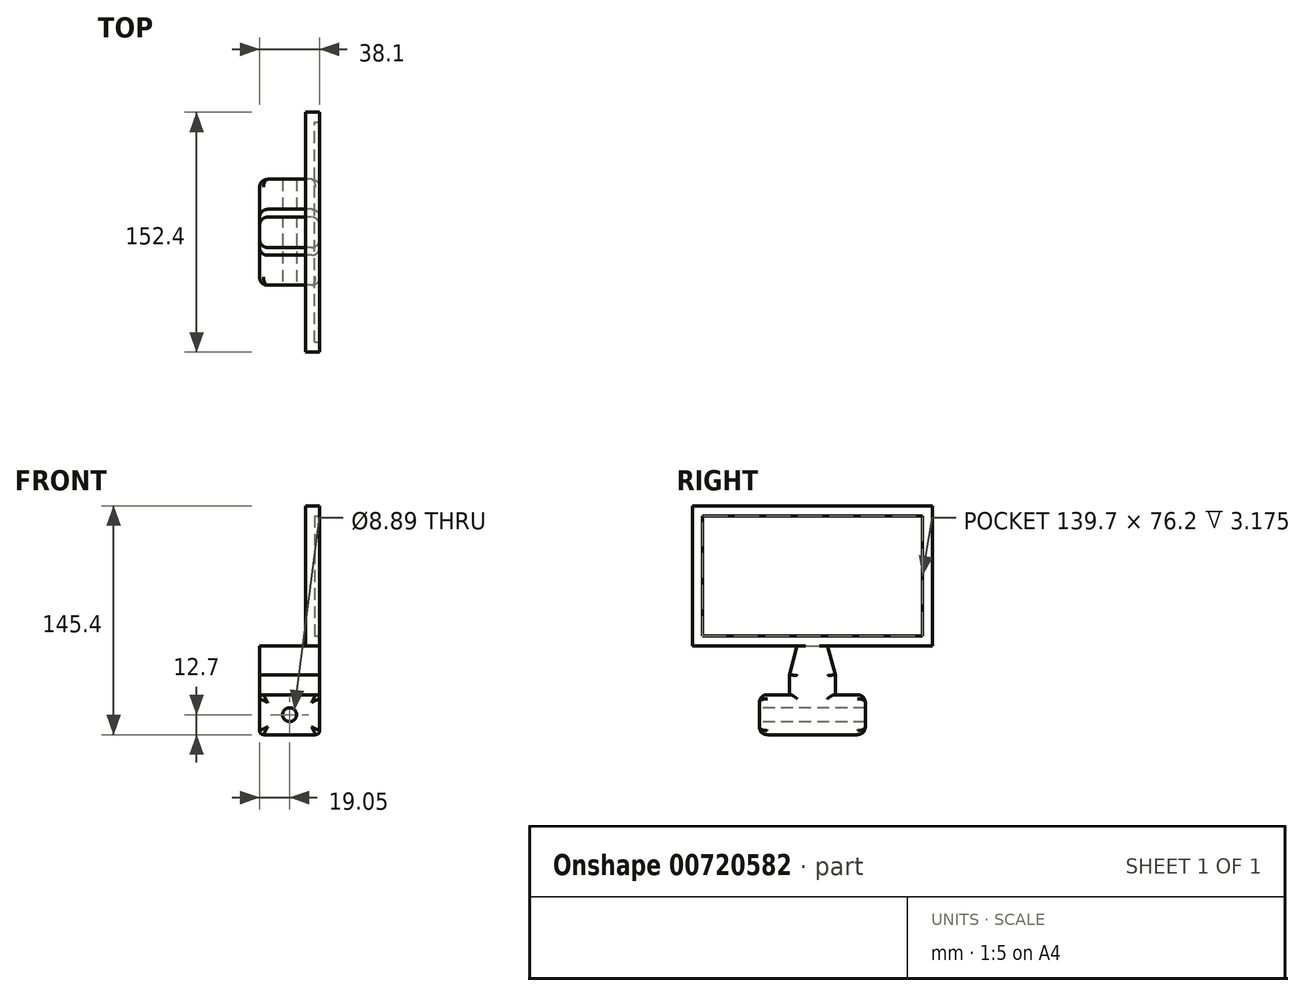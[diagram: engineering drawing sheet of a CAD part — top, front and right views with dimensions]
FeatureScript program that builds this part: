
annotation { "Feature Type Name" : "Feature", "Feature Type Description" : "" }
export const myFeature = defineFeature(function(context is Context, id is Id, definition is map)
    precondition{}
    {
        {
            var Q0;
            Q0=qCreatedBy(makeId("Right.planeOp"),FACE);
            var sketch = newSketch(context, id + "F0", { "sketchPlane" : qUnion([Q0])});
            skLineSegment(sketch, "E0.top", {"start": v(-67.31, 0) * mm, "end": v(0, 0) * mm});
            skLineSegment(sketch, "E0.left", {"start": v(-67.31, 25.4) * mm, "end": v(-67.31, 0) * mm});
            skLineSegment(sketch, "E0.right", {"start": v(0, 25.4) * mm, "end": v(0, 0) * mm});
            skLineSegment(sketch, "E1", {"start": v(-67.31, 25.4) * mm, "end": v(-48.26, 25.4) * mm});
            skLineSegment(sketch, "E2", {"start": v(0, 25.4) * mm, "end": v(-19.05, 25.4) * mm});
            skLineSegment(sketch, "E3", {"start": v(-48.26, 25.4) * mm, "end": v(-48.26, 38.1) * mm});
            skLineSegment(sketch, "E4", {"start": v(-19.05, 25.4) * mm, "end": v(-19.05, 38.1) * mm});
            skLineSegment(sketch, "E5", {"start": v(-48.26, 38.1) * mm, "end": v(-43.33, 56.5) * mm});
            skLineSegment(sketch, "E6", {"start": v(-19.05, 38.1) * mm, "end": v(-23.98, 56.5) * mm});
            skLineSegment(sketch, "E7", {"start": v(-43.33, 56.5) * mm, "end": v(-23.98, 56.5) * mm});
            skSolve(sketch);
        }
        {
            var Q0;
            Q0=makeQuery(id+"F0.imprint","IMPRINT",FACE,{"disambiguationData":[TD([[makeQuery(id+"F0.imprint","IMPRINT",EDGE,{"derivedFrom":sQuery(id+"F0.wireOp",EDGE,"E0.top")}),1.0]])]});
            extrude(context, id + "F1", {"entities" : qUnion([Q0]), "depth" : 38.1 * mm, "offsetDistance" : 25.4 * mm});
        }
        {
            var Q0;
            Q0=makeQuery(id+"F1.opExtrude","SWEPT_EDGE",EDGE,{"disambiguationData":[OSD([sQuery(id+"F0.wireOp",EDGE,"E0.left"),sQuery(id+"F0.wireOp",EDGE,"E1")])]});
            var Q1;
            Q1=makeQuery(id+"F1.opExtrude","CAP_EDGE",EDGE,{"disambiguationData":[OSD([sQuery(id+"F0.wireOp",EDGE,"E0.left")])],"isStart":false});
            var Q2;
            Q2=makeQuery(id+"F1.opExtrude","SWEPT_EDGE",EDGE,{"disambiguationData":[OSD([sQuery(id+"F0.wireOp",EDGE,"E0.top"),sQuery(id+"F0.wireOp",EDGE,"E0.left")])]});
            var Q3;
            Q3=makeQuery(id+"F1.opExtrude","SWEPT_FACE",FACE,{"disambiguationData":[OSD([sQuery(id+"F0.wireOp",EDGE,"E0.left")])]});
            var Q4;
            Q4=makeQuery(id+"F1.opExtrude","CAP_EDGE",EDGE,{"disambiguationData":[OSD([sQuery(id+"F0.wireOp",EDGE,"E0.right")])],"isStart":false});
            var Q5;
            Q5=makeQuery(id+"F1.opExtrude","SWEPT_EDGE",EDGE,{"disambiguationData":[OSD([sQuery(id+"F0.wireOp",EDGE,"E0.right"),sQuery(id+"F0.wireOp",EDGE,"E2")])]});
            var Q6;
            Q6=makeQuery(id+"F1.opExtrude","CAP_EDGE",EDGE,{"disambiguationData":[OSD([sQuery(id+"F0.wireOp",EDGE,"E0.right")])],"isStart":true});
            var Q7;
            Q7=makeQuery(id+"F1.opExtrude","SWEPT_EDGE",EDGE,{"disambiguationData":[OSD([sQuery(id+"F0.wireOp",EDGE,"E0.top"),sQuery(id+"F0.wireOp",EDGE,"E0.right")])]});
            fillet(context, id + "F2", {"entities" : qUnion([Q0, Q1, Q2, Q3, Q4, Q5, Q6, Q7]), "radius" : 5.08 * mm, "tangentPropagation" : true, "allowEdgeOverflow" : false});
        }
        {
            var Q0;
            Q0=makeQuery(id+"F1.opExtrude","SWEPT_FACE",FACE,{"disambiguationData":[OSD([sQuery(id+"F0.wireOp",EDGE,"E0.left")])]});
            var sketch = newSketch(context, id + "F3", { "sketchPlane" : qUnion([Q0])});
            skPoint(sketch, "E8", {"position": v(19.05, 12.7) * mm});
            skPoint(sketch, "E8.positionSnap0", {"position": v(19.05, 5.08) * mm});
            skSolve(sketch);
        }
        {
            var Q0;
            Q0=sQuery(id+"F3.wireOp",VERTEX,"E8");
            var Q1;
            Q1=makeQuery(id+"F1.opExtrude","SWEPT_BODY",BODY,{"disambiguationData":[OSD([sQuery(id+"F0.wireOp",EDGE,"E0.top"),sQuery(id+"F0.wireOp",EDGE,"E0.left"),sQuery(id+"F0.wireOp",EDGE,"E0.right"),sQuery(id+"F0.wireOp",EDGE,"E1"),sQuery(id+"F0.wireOp",EDGE,"E2"),sQuery(id+"F0.wireOp",EDGE,"E3"),sQuery(id+"F0.wireOp",EDGE,"E4"),sQuery(id+"F0.wireOp",EDGE,"E5"),sQuery(id+"F0.wireOp",EDGE,"E6"),sQuery(id+"F0.wireOp",EDGE,"E7")])]});
            hole(context, id + "F4", {"style" : HoleStyle.SIMPLE, "endStyle" : HoleEndStyle.THROUGH, "holeDiameter" : 8.9 * mm, "majorDiameter" : 6.35 * mm, "isTappedThrough" : true, "tappedDepth" : 12.7 * mm, "tapClearance" : 3, "startFromSketch" : true, "locations" : qUnion([Q0]), "scope" : qUnion([Q1])});
        }
        {
            var Q0;
            Q0=makeQuery(id+"F1.opExtrude","CAP_EDGE",EDGE,{"disambiguationData":[OSD([sQuery(id+"F0.wireOp",EDGE,"E3")])],"isStart":false});
            var Q1;
            Q1=makeQuery(id+"F1.opExtrude","CAP_EDGE",EDGE,{"disambiguationData":[OSD([sQuery(id+"F0.wireOp",EDGE,"E5")])],"isStart":false});
            var Q2;
            Q2=makeQuery(id+"F1.opExtrude","CAP_EDGE",EDGE,{"disambiguationData":[OSD([sQuery(id+"F0.wireOp",EDGE,"E6")])],"isStart":false});
            var Q3;
            Q3=makeQuery(id+"F1.opExtrude","CAP_EDGE",EDGE,{"disambiguationData":[OSD([sQuery(id+"F0.wireOp",EDGE,"E4")])],"isStart":false});
            var Q4;
            Q4=makeQuery(id+"F1.opExtrude","CAP_EDGE",EDGE,{"disambiguationData":[OSD([sQuery(id+"F0.wireOp",EDGE,"E3")])],"isStart":true});
            var Q5;
            Q5=makeQuery(id+"F1.opExtrude","CAP_EDGE",EDGE,{"disambiguationData":[OSD([sQuery(id+"F0.wireOp",EDGE,"E5")])],"isStart":true});
            var Q6;
            Q6=makeQuery(id+"F1.opExtrude","CAP_EDGE",EDGE,{"disambiguationData":[OSD([sQuery(id+"F0.wireOp",EDGE,"E4")])],"isStart":true});
            var Q7;
            Q7=makeQuery(id+"F1.opExtrude","CAP_EDGE",EDGE,{"disambiguationData":[OSD([sQuery(id+"F0.wireOp",EDGE,"E6")])],"isStart":true});
            fillet(context, id + "F5", {"entities" : qUnion([Q0, Q1, Q2, Q3, Q4, Q5, Q6, Q7]), "radius" : 5.08 * mm, "tangentPropagation" : true, "allowEdgeOverflow" : false});
        }
        {
            var Q0;
            Q0=makeQuery(id+"F1.opExtrude","CAP_FACE",FACE,{"disambiguationData":[OSD([sQuery(id+"F0.wireOp",EDGE,"E0.top"),sQuery(id+"F0.wireOp",EDGE,"E0.left"),sQuery(id+"F0.wireOp",EDGE,"E0.right"),sQuery(id+"F0.wireOp",EDGE,"E1"),sQuery(id+"F0.wireOp",EDGE,"E2"),sQuery(id+"F0.wireOp",EDGE,"E3"),sQuery(id+"F0.wireOp",EDGE,"E4"),sQuery(id+"F0.wireOp",EDGE,"E5"),sQuery(id+"F0.wireOp",EDGE,"E6"),sQuery(id+"F0.wireOp",EDGE,"E7")])],"isStart":false});
            var sketch = newSketch(context, id + "F6", { "sketchPlane" : qUnion([Q0])});
            skLineSegment(sketch, "E9.bottom", {"start": v(-109.86, 56.5) * mm, "end": v(42.55, 56.5) * mm});
            skLineSegment(sketch, "E9.top", {"start": v(-109.86, 145.4) * mm, "end": v(42.55, 145.4) * mm});
            skLineSegment(sketch, "E9.left", {"start": v(-109.85, 56.5) * mm, "end": v(-109.86, 145.4) * mm});
            skLineSegment(sketch, "E9.right", {"start": v(42.55, 56.5) * mm, "end": v(42.55, 145.4) * mm});
            skSolve(sketch);
        }
        {
            var Q0;
            Q0=makeQuery(id+"F6.imprint","IMPRINT",FACE,{"disambiguationData":[TD([[makeQuery(id+"F6.imprint","IMPRINT",EDGE,{"derivedFrom":sQuery(id+"F6.wireOp",EDGE,"E9.top")}),-1.0]])]});
            extrude(context, id + "F7", {"entities" : qUnion([Q0]), "operationType" : NewBodyOperationType.ADD, "oppositeDirection" : true, "depth" : 8.9 * mm, "offsetDistance" : 25.4 * mm});
        }
        {
            var Q0;
            Q0=makeQuery(id+"F7.boolean.opBoolean","MERGE",FACE,{"derivedFrom":[makeQuery(id+"F1.opExtrude","CAP_FACE",FACE,{"disambiguationData":[OSD([sQuery(id+"F0.wireOp",EDGE,"E0.top"),sQuery(id+"F0.wireOp",EDGE,"E0.left"),sQuery(id+"F0.wireOp",EDGE,"E0.right"),sQuery(id+"F0.wireOp",EDGE,"E1"),sQuery(id+"F0.wireOp",EDGE,"E2"),sQuery(id+"F0.wireOp",EDGE,"E3"),sQuery(id+"F0.wireOp",EDGE,"E4"),sQuery(id+"F0.wireOp",EDGE,"E5"),sQuery(id+"F0.wireOp",EDGE,"E6"),sQuery(id+"F0.wireOp",EDGE,"E7")])],"isStart":false}),makeQuery(id+"F7.opExtrude","CAP_FACE",FACE,{"disambiguationData":[OSD([sQuery(id+"F6.wireOp",EDGE,"E9.bottom"),sQuery(id+"F6.wireOp",EDGE,"E9.top"),sQuery(id+"F6.wireOp",EDGE,"E9.left"),sQuery(id+"F6.wireOp",EDGE,"E9.right")])],"isStart":true})]});
            var sketch = newSketch(context, id + "F8", { "sketchPlane" : qUnion([Q0])});
            skLineSegment(sketch, "E10.bottom", {"start": v(-103.5, 139.05) * mm, "end": v(36.2, 139.05) * mm});
            skLineSegment(sketch, "E10.top", {"start": v(-103.5, 62.85) * mm, "end": v(36.2, 62.85) * mm});
            skLineSegment(sketch, "E10.left", {"start": v(-103.5, 139.05) * mm, "end": v(-103.5, 62.85) * mm});
            skLineSegment(sketch, "E10.right", {"start": v(36.2, 139.05) * mm, "end": v(36.2, 62.85) * mm});
            skSolve(sketch);
        }
        {
            var Q0;
            Q0=makeQuery(id+"F8.imprint","IMPRINT",FACE,{"disambiguationData":[TD([[makeQuery(id+"F8.imprint","IMPRINT",EDGE,{"derivedFrom":sQuery(id+"F8.wireOp",EDGE,"E10.bottom")}),-1.0]])]});
            extrude(context, id + "F9", {"entities" : qUnion([Q0]), "operationType" : NewBodyOperationType.REMOVE, "oppositeDirection" : true, "depth" : 3.17 * mm, "offsetDistance" : 25.4 * mm});
        }
        {
            var Q0;
            Q0=makeQuery(id+"F1.opExtrude","CAP_EDGE",EDGE,{"disambiguationData":[OSD([sQuery(id+"F0.wireOp",EDGE,"E1")])],"isStart":false});
            var Q1;
            Q1=makeQuery(id+"F1.opExtrude","CAP_EDGE",EDGE,{"disambiguationData":[OSD([sQuery(id+"F0.wireOp",EDGE,"E2")])],"isStart":false});
            var Q2;
            Q2=makeQuery(id+"F1.opExtrude","CAP_EDGE",EDGE,{"disambiguationData":[OSD([sQuery(id+"F0.wireOp",EDGE,"E0.top")])],"isStart":false});
            fillet(context, id + "F10", {"entities" : qUnion([Q0, Q1, Q2]), "radius" : 2.54 * mm, "tangentPropagation" : true, "allowEdgeOverflow" : false});
        }
        {
            var Q0;
            Q0=makeQuery(id+"F1.opExtrude","CAP_EDGE",EDGE,{"disambiguationData":[OSD([sQuery(id+"F0.wireOp",EDGE,"E1")])],"isStart":true});
            var Q1;
            Q1=makeQuery(id+"F1.opExtrude","CAP_EDGE",EDGE,{"disambiguationData":[OSD([sQuery(id+"F0.wireOp",EDGE,"E2")])],"isStart":true});
            var Q2;
            Q2=makeQuery(id+"F1.opExtrude","CAP_EDGE",EDGE,{"disambiguationData":[OSD([sQuery(id+"F0.wireOp",EDGE,"E0.top")])],"isStart":true});
            fillet(context, id + "F11", {"entities" : qUnion([Q0, Q1, Q2]), "radius" : 2.54 * mm, "tangentPropagation" : true, "allowEdgeOverflow" : false});
        }
    });
